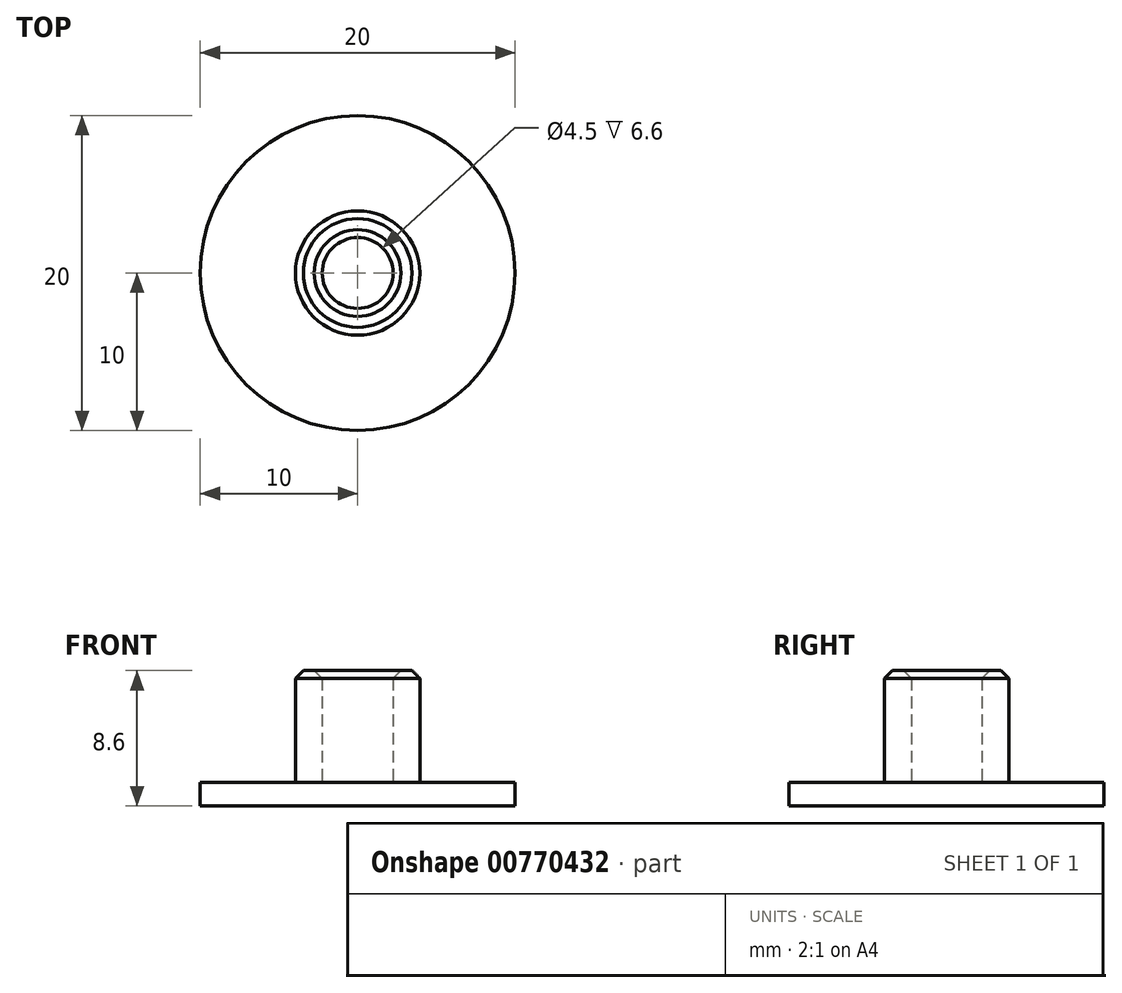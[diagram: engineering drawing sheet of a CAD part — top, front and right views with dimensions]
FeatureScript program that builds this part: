
annotation { "Feature Type Name" : "Feature", "Feature Type Description" : "" }
export const myFeature = defineFeature(function(context is Context, id is Id, definition is map)
    precondition{}
    {
        {
            var Q0;
            Q0=qCreatedBy(makeId("Top.planeOp"),FACE);
            var sketch = newSketch(context, id + "F0", { "sketchPlane" : qUnion([Q0])});
            skCircle(sketch, "E0", {"center": v(0, 0) * mm, "radius": 10 * mm});
            skSolve(sketch);
        }
        {
            var Q0;
            Q0 = qSketchRegion(id + "F0", true);
            extrude(context, id + "F1", {"entities" : qUnion([Q0]), "depth" : 1.5 * mm, "offsetDistance" : 25 * mm});
        }
        {
            var Q0;
            Q0=makeQuery(id+"F1.opExtrude","CAP_FACE",FACE,{"disambiguationData":[OSD([sQuery(id+"F0.wireOp",EDGE,"E0")])],"isStart":false});
            var sketch = newSketch(context, id + "F2", { "sketchPlane" : qUnion([Q0])});
            skCircle(sketch, "E1", {"center": v(0, 0) * mm, "radius": 3.95 * mm});
            skCircle(sketch, "E2", {"center": v(0, 0) * mm, "radius": 2.25 * mm});
            skSolve(sketch);
        }
        {
            var Q0;
            Q0 = qSketchRegion(id + "F2", true);
            extrude(context, id + "F3", {"entities" : qUnion([Q0]), "operationType" : NewBodyOperationType.ADD, "depth" : 7.1 * mm, "offsetDistance" : 25 * mm});
        }
        {
            var Q0;
            Q0=makeQuery(id+"F3.opExtrude","CAP_EDGE",EDGE,{"disambiguationData":[OSD([sQuery(id+"F2.wireOp",EDGE,"E1")])],"isStart":false});
            var Q1;
            Q1=makeQuery(id+"F3.opExtrude","CAP_EDGE",EDGE,{"disambiguationData":[OSD([sQuery(id+"F2.wireOp",EDGE,"E2")])],"isStart":false});
            chamfer(context, id + "F4", {"entities" : qUnion([Q0, Q1]), "width" : .5 * mm, "tangentPropagation" : true});
        }
    });
